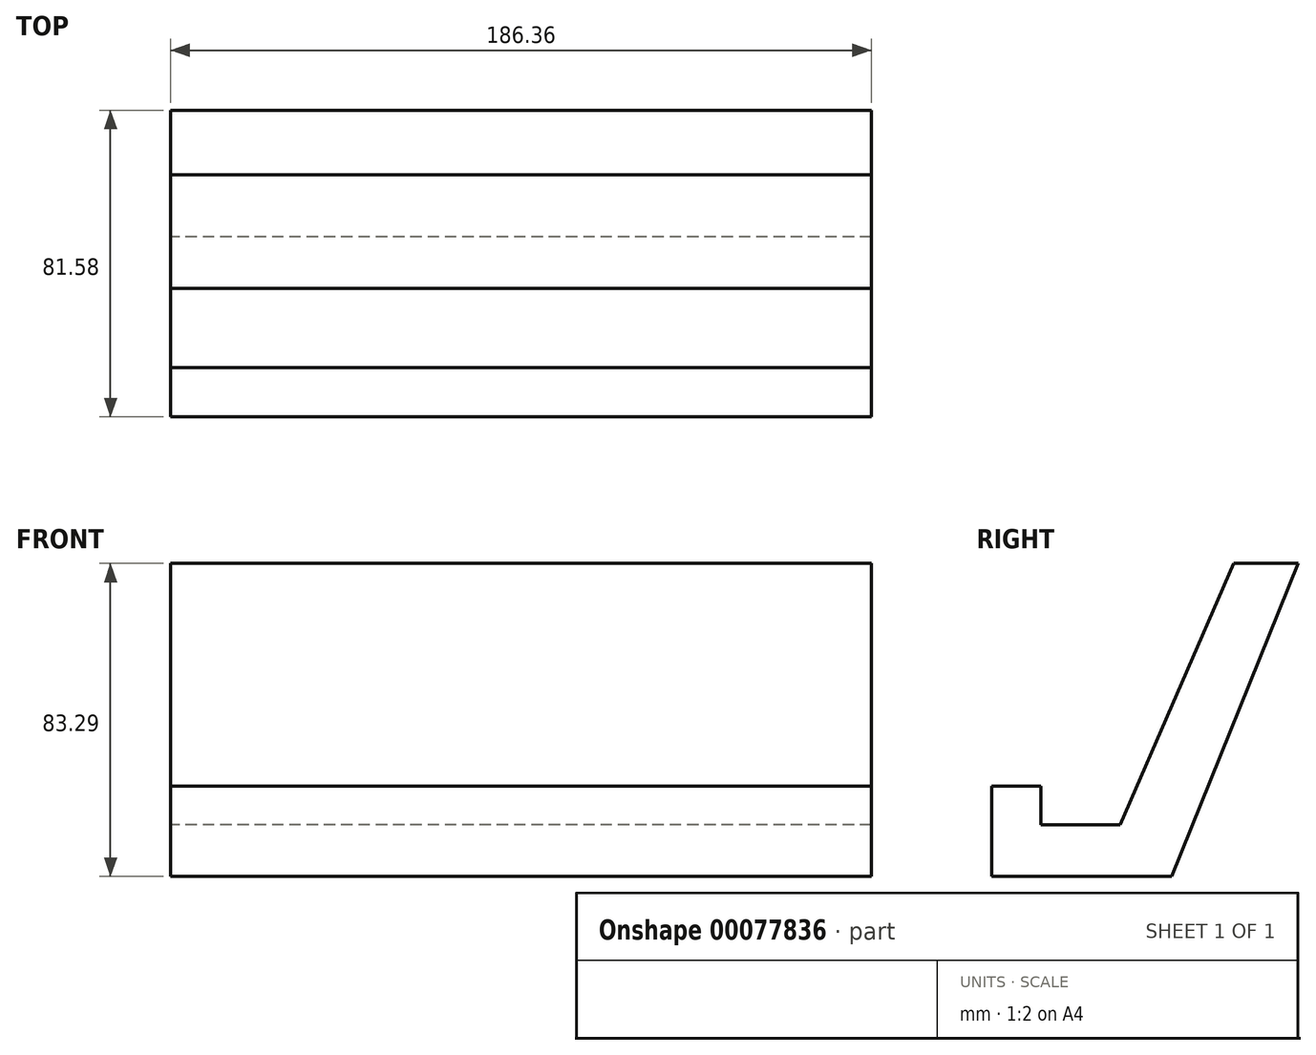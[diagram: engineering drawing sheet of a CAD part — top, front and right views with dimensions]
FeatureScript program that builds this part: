
annotation { "Feature Type Name" : "Feature", "Feature Type Description" : "" }
export const myFeature = defineFeature(function(context is Context, id is Id, definition is map)
    precondition{}
    {
        {
            var Q0;
            Q0=qCreatedBy(makeId("Right.planeOp"),FACE);
            var sketch = newSketch(context, id + "F0", { "sketchPlane" : qUnion([Q0])});
            skLineSegment(sketch, "E0", {"start": v(37.37, 44.35) * mm, "end": v(7.13, -25.24) * mm});
            skLineSegment(sketch, "E1", {"start": v(7.13, -25.24) * mm, "end": v(-13.98, -25.24) * mm});
            skLineSegment(sketch, "E2", {"start": v(-13.98, -25.24) * mm, "end": v(-13.98, -14.98) * mm});
            skLineSegment(sketch, "E3", {"start": v(-13.98, -14.98) * mm, "end": v(-27.1, -14.98) * mm});
            skLineSegment(sketch, "E4", {"start": v(-27.1, -14.98) * mm, "end": v(-27.1, -38.94) * mm});
            skLineSegment(sketch, "E5", {"start": v(-27.1, -38.94) * mm, "end": v(20.82, -38.94) * mm});
            skLineSegment(sketch, "E6", {"start": v(20.82, -38.94) * mm, "end": v(54.48, 44.35) * mm});
            skLineSegment(sketch, "E7", {"start": v(54.48, 44.35) * mm, "end": v(37.37, 44.35) * mm});
            skSolve(sketch);
        }
        {
            var Q0;
            Q0 = qSketchRegion(id + "F0", true);
            extrude(context, id + "F1", {"entities" : qUnion([Q0]), "depth" : 186.36 * mm});
        }
    });
